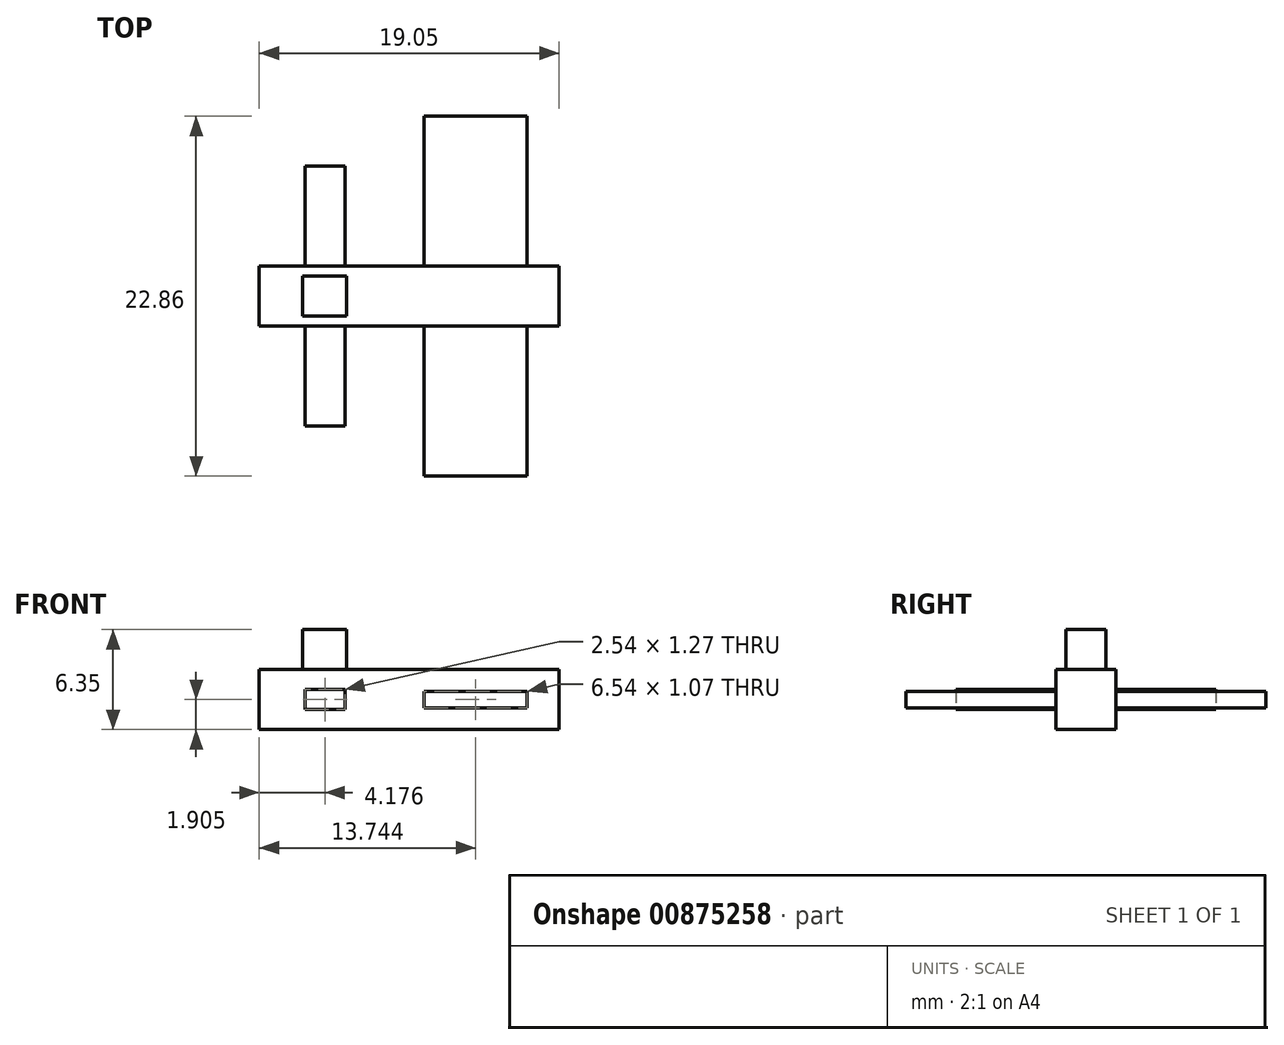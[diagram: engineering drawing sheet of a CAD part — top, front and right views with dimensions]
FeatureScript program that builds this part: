
annotation { "Feature Type Name" : "Feature", "Feature Type Description" : "" }
export const myFeature = defineFeature(function(context is Context, id is Id, definition is map)
    precondition{}
    {
        {
            var Q0;
            Q0=qCreatedBy(makeId("Top.planeOp"),FACE);
            var sketch = newSketch(context, id + "F0", { "sketchPlane" : qUnion([Q0])});
            skLineSegment(sketch, "E0.bottom", {"start": v(-65.76, 4.05) * mm, "end": v(-46.71, 4.05) * mm});
            skLineSegment(sketch, "E0.top", {"start": v(-65.76, 5.95) * mm, "end": v(-46.71, 5.95) * mm});
            skLineSegment(sketch, "E0.left", {"start": v(-65.76, 4.05) * mm, "end": v(-65.76, 5.95) * mm});
            skLineSegment(sketch, "E0.right", {"start": v(-46.71, 4.05) * mm, "end": v(-46.71, 5.95) * mm});
            skSolve(sketch);
        }
        {
            var Q0;
            Q0=qSketchRegion(id+"F0",true);
            extrude(context, id + "F1", {"entities" : qUnion([Q0]), "depth" : 3.8 * mm, "offsetDistance" : 25.4 * mm});
        }
        {
            var Q0;
            Q0=makeQuery(id+"F1.opExtrude","SWEPT_FACE",FACE,{"disambiguationData":[OSD([sQuery(id+"F0.wireOp",EDGE,"E0.top")])]});
            var sketch = newSketch(context, id + "F2", { "sketchPlane" : qUnion([Q0])});
            skLineSegment(sketch, "E1.bottom", {"start": v(48.75, 1.37) * mm, "end": v(55.29, 1.37) * mm});
            skLineSegment(sketch, "E1.top", {"start": v(48.75, 2.44) * mm, "end": v(55.29, 2.44) * mm});
            skLineSegment(sketch, "E1.left", {"start": v(48.75, 2.44) * mm, "end": v(48.75, 1.37) * mm});
            skLineSegment(sketch, "E1.right", {"start": v(55.29, 2.44) * mm, "end": v(55.29, 1.37) * mm});
            skSolve(sketch);
        }
        {
            var Q0;
            Q0=qSketchRegion(id+"F2",true);
            extrude(context, id + "F3", {"entities" : qUnion([Q0]), "operationType" : NewBodyOperationType.ADD, "depth" : 9.52 * mm, "offsetDistance" : 25.4 * mm});
        }
        {
            var Q0;
            Q0=makeQuery(id+"F1.opExtrude","SWEPT_FACE",FACE,{"disambiguationData":[OSD([sQuery(id+"F0.wireOp",EDGE,"E0.top")])]});
            var sketch = newSketch(context, id + "F4", { "sketchPlane" : qUnion([Q0])});
            skLineSegment(sketch, "E2.bottom", {"start": v(60.31, 2.54) * mm, "end": v(62.85, 2.54) * mm});
            skLineSegment(sketch, "E2.top", {"start": v(60.31, 1.27) * mm, "end": v(62.85, 1.27) * mm});
            skLineSegment(sketch, "E2.left", {"start": v(60.31, 2.54) * mm, "end": v(60.31, 1.27) * mm});
            skLineSegment(sketch, "E2.right", {"start": v(62.85, 2.54) * mm, "end": v(62.85, 1.27) * mm});
            skSolve(sketch);
        }
        {
            var Q0;
            Q0=qSketchRegion(id+"F4",true);
            extrude(context, id + "F5", {"entities" : qUnion([Q0]), "operationType" : NewBodyOperationType.ADD, "depth" : 6.35 * mm, "offsetDistance" : 25.4 * mm});
        }
        {
            var Q0;
            Q0=makeQuery(id+"F1.opExtrude","CAP_FACE",FACE,{"disambiguationData":[OSD([sQuery(id+"F0.wireOp",EDGE,"E0.bottom"),sQuery(id+"F0.wireOp",EDGE,"E0.top"),sQuery(id+"F0.wireOp",EDGE,"E0.left"),sQuery(id+"F0.wireOp",EDGE,"E0.right")])],"isStart":false});
            var sketch = newSketch(context, id + "F6", { "sketchPlane" : qUnion([Q0])});
            skLineSegment(sketch, "E3.bottom", {"start": v(-63, 4.05) * mm, "end": v(-60.23, 4.05) * mm});
            skLineSegment(sketch, "E3.top", {"start": v(-63, 5.32) * mm, "end": v(-60.23, 5.32) * mm});
            skLineSegment(sketch, "E3.left", {"start": v(-63, 4.05) * mm, "end": v(-63, 5.32) * mm});
            skLineSegment(sketch, "E3.right", {"start": v(-60.23, 4.05) * mm, "end": v(-60.23, 5.32) * mm});
            skSolve(sketch);
        }
        {
            var Q0;
            Q0=qSketchRegion(id+"F6",true);
            extrude(context, id + "F7", {"entities" : qUnion([Q0]), "operationType" : NewBodyOperationType.ADD, "depth" : 2.54 * mm, "offsetDistance" : 25.4 * mm});
        }
        {
            var Q0;
            Q0=makeQuery(id+"F1.opExtrude","SWEPT_BODY",BODY,{"disambiguationData":[OSD([sQuery(id+"F0.wireOp",EDGE,"E0.bottom"),sQuery(id+"F0.wireOp",EDGE,"E0.top"),sQuery(id+"F0.wireOp",EDGE,"E0.left"),sQuery(id+"F0.wireOp",EDGE,"E0.right")])]});
            var Q1;
            Q1=makeQuery(id+"F7.boolean.opBoolean","MERGE",FACE,{"derivedFrom":[makeQuery(id+"F1.opExtrude","SWEPT_FACE",FACE,{"disambiguationData":[OSD([sQuery(id+"F0.wireOp",EDGE,"E0.bottom")])]}),makeQuery(id+"F7.opExtrude","SWEPT_FACE",FACE,{"disambiguationData":[OSD([sQuery(id+"F6.wireOp",EDGE,"E3.bottom")])]})]});
            mirror(context, id + "F8", {"operationType" : NewBodyOperationType.ADD, "entities" : qUnion([Q0]), "mirrorPlane" : qUnion([Q1])});
        }
    });
